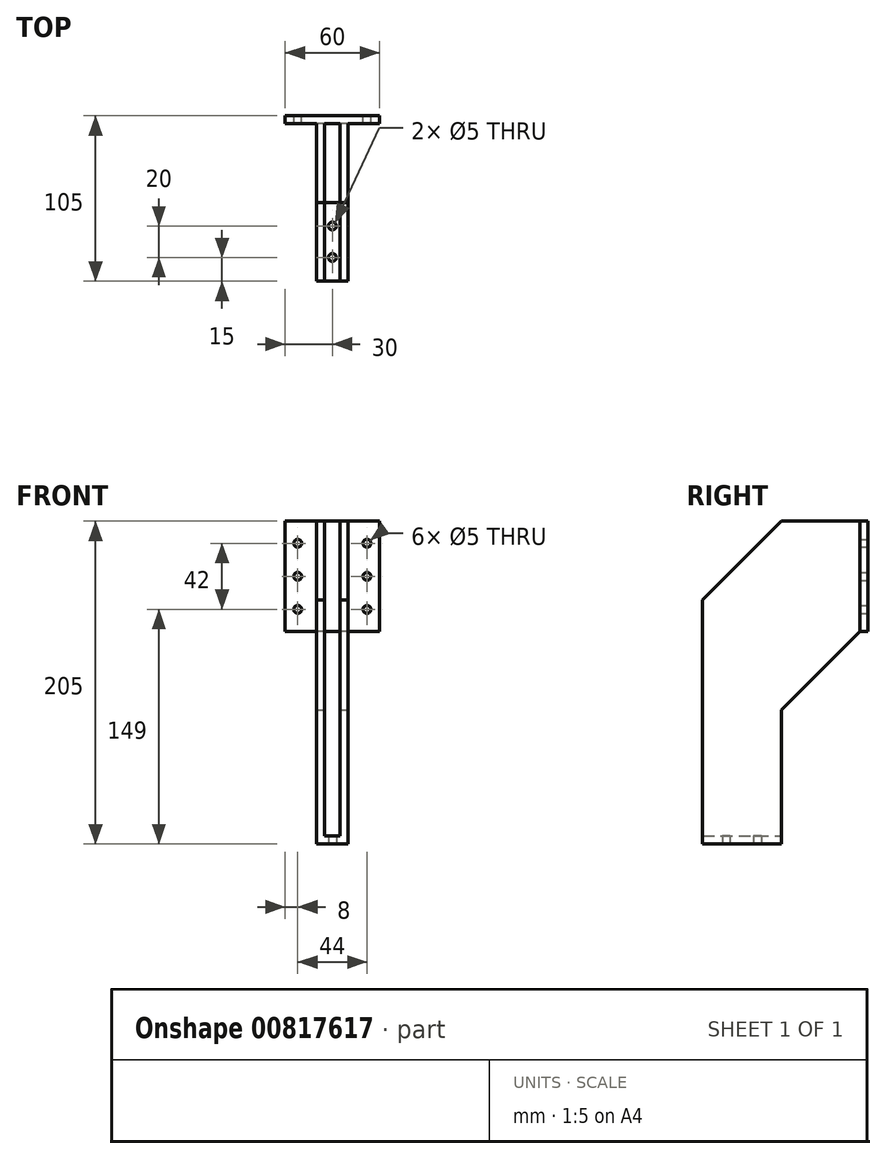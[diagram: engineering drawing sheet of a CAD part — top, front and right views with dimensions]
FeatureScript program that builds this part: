
annotation { "Feature Type Name" : "Feature", "Feature Type Description" : "" }
export const myFeature = defineFeature(function(context is Context, id is Id, definition is map)
    precondition{}
    {
        {
            var Q0;
            Q0=qCreatedBy(makeId("Front.planeOp"),FACE);
            var sketch = newSketch(context, id + "F0", { "sketchPlane" : qUnion([Q0])});
            skLineSegment(sketch, "E0.bottom", {"start": v(30, 35) * mm, "end": v(-30, 35) * mm});
            skLineSegment(sketch, "E0.top", {"start": v(30, -35) * mm, "end": v(-30, -35) * mm});
            skLineSegment(sketch, "E0.left", {"start": v(30, 35) * mm, "end": v(30, -35) * mm});
            skLineSegment(sketch, "E0.right", {"start": v(-30, 35) * mm, "end": v(-30, -35) * mm});
            skPoint(sketch, "E0.middle", {"position": v(0, 0) * mm});
            skCircle(sketch, "E1", {"center": v(-22, 21) * mm, "radius": 2.5 * mm});
            skCircle(sketch, "E2", {"center": v(-22, 0) * mm, "radius": 2.5 * mm});
            skCircle(sketch, "E3", {"center": v(-22, -21) * mm, "radius": 2.5 * mm});
            skCircle(sketch, "E4", {"center": v(22, 21) * mm, "radius": 2.5 * mm});
            skCircle(sketch, "E5", {"center": v(22, 0) * mm, "radius": 2.5 * mm});
            skCircle(sketch, "E6", {"center": v(22, -21) * mm, "radius": 2.5 * mm});
            skSolve(sketch);
        }
        {
            var Q0;
            Q0=makeQuery(id+"F0.imprint","IMPRINT",FACE,{"disambiguationData":[TD([[makeQuery(id+"F0.imprint","IMPRINT",EDGE,{"derivedFrom":sQuery(id+"F0.wireOp",EDGE,"E0.bottom")}),1.0]])]});
            extrude(context, id + "F1", {"entities" : qUnion([Q0]), "depth" : 5 * mm, "offsetDistance" : 25 * mm});
        }
        {
            var Q0;
            Q0=makeQuery(id+"F1.opExtrude","CAP_FACE",FACE,{"disambiguationData":[OSD([sQuery(id+"F0.wireOp",EDGE,"E0.bottom"),sQuery(id+"F0.wireOp",EDGE,"E0.top"),sQuery(id+"F0.wireOp",EDGE,"E0.left"),sQuery(id+"F0.wireOp",EDGE,"E0.right"),sQuery(id+"F0.wireOp",EDGE,"E1"),sQuery(id+"F0.wireOp",EDGE,"E2"),sQuery(id+"F0.wireOp",EDGE,"E3"),sQuery(id+"F0.wireOp",EDGE,"E4"),sQuery(id+"F0.wireOp",EDGE,"E5"),sQuery(id+"F0.wireOp",EDGE,"E6")])],"isStart":false});
            var sketch = newSketch(context, id + "F2", { "sketchPlane" : qUnion([Q0])});
            skLineSegment(sketch, "E7.bottom", {"start": v(-10, 35) * mm, "end": v(-5, 35) * mm});
            skLineSegment(sketch, "E7.top", {"start": v(-10, -165) * mm, "end": v(-5, -165) * mm});
            skLineSegment(sketch, "E7.left", {"start": v(-10, 35) * mm, "end": v(-10, -165) * mm});
            skLineSegment(sketch, "E7.right", {"start": v(-5, 35) * mm, "end": v(-5, -165) * mm});
            skLineSegment(sketch, "E8.bottom", {"start": v(5, 35) * mm, "end": v(10, 35) * mm});
            skLineSegment(sketch, "E8.top", {"start": v(5, -165) * mm, "end": v(10, -165) * mm});
            skLineSegment(sketch, "E8.left", {"start": v(5, 35) * mm, "end": v(5, -165) * mm});
            skLineSegment(sketch, "E8.right", {"start": v(10, 35) * mm, "end": v(10, -165) * mm});
            skSolve(sketch);
        }
        {
            var Q0;
            {var subQ0=sQuery(id+"F2.wireOp",EDGE,"E7.top");Q0=makeQuery(id+"F2.imprint","IMPRINT",FACE,{"disambiguationData":[TD([[makeQuery(id+"F2.imprint","IMPRINT",EDGE,{"derivedFrom":subQ0}),1.0]])]});}
            var Q1;
            {var subQ0=sQuery(id+"F2.wireOp",EDGE,"E7.bottom");Q1=makeQuery(id+"F2.imprint","IMPRINT",FACE,{"disambiguationData":[TD([[makeQuery(id+"F2.imprint","IMPRINT",EDGE,{"derivedFrom":subQ0}),-1.0]])]});}
            var Q2;
            {var subQ0=sQuery(id+"F2.wireOp",EDGE,"E8.bottom");Q2=makeQuery(id+"F2.imprint","IMPRINT",FACE,{"disambiguationData":[TD([[makeQuery(id+"F2.imprint","IMPRINT",EDGE,{"derivedFrom":subQ0}),-1.0]])]});}
            var Q3;
            {var subQ0=sQuery(id+"F2.wireOp",EDGE,"E8.top");Q3=makeQuery(id+"F2.imprint","IMPRINT",FACE,{"disambiguationData":[TD([[makeQuery(id+"F2.imprint","IMPRINT",EDGE,{"derivedFrom":subQ0}),1.0]])]});}
            var Q4;
            {var subQ0=sQuery(id+"F2.wireOp",EDGE,"E7.bottom");Q4=makeQuery(id+"F2.imprint","IMPRINT",FACE,{"disambiguationData":[TD([[makeQuery(id+"F2.imprint","IMPRINT",EDGE,{"derivedFrom":subQ0}),1.0]])]});}
            var Q5;
            {var subQ0=sQuery(id+"F2.wireOp",EDGE,"E8.bottom");Q5=makeQuery(id+"F2.imprint","IMPRINT",FACE,{"disambiguationData":[TD([[makeQuery(id+"F2.imprint","IMPRINT",EDGE,{"derivedFrom":subQ0}),1.0]])]});}
            extrude(context, id + "F3", {"entities" : qUnion([Q0, Q1, Q2, Q3, Q4, Q5]), "operationType" : NewBodyOperationType.ADD, "depth" : 100 * mm, "offsetDistance" : 25 * mm});
        }
        {
            var Q0;
            Q0=makeQuery(id+"F3.opExtrude","SWEPT_FACE",FACE,{"disambiguationData":[OSD([sQuery(id+"F2.wireOp",EDGE,"E8.right")])]});
            var sketch = newSketch(context, id + "F4", { "sketchPlane" : qUnion([Q0])});
            skPoint(sketch, "E9.start.orphan", {"position": v(-5, -35) * mm});
            skLineSegment(sketch, "E10", {"start": v(-55, 35) * mm, "end": v(-55, -165) * mm, "construction": true});
            skLineSegment(sketch, "E11", {"start": v(-105, -15) * mm, "end": v(-5, -15) * mm, "construction": true});
            skLineSegment(sketch, "E12", {"start": v(-55, 35) * mm, "end": v(-105, -15) * mm});
            skLineSegment(sketch, "E13", {"start": v(-105, -85) * mm, "end": v(-5, -85) * mm, "construction": true});
            skLineSegment(sketch, "E14", {"start": v(-5, -35) * mm, "end": v(-55, -85) * mm});
            skLineSegment(sketch, "E15", {"start": v(-55, -85) * mm, "end": v(-55, -165) * mm});
            skSolve(sketch);
        }
        {
            var Q0;
            {var subQ0=sQuery(id+"F4.wireOp",EDGE,"E12");Q0=makeQuery(id+"F4.imprint","IMPRINT",FACE,{"disambiguationData":[TD([[makeQuery(id+"F4.imprint","IMPRINT",EDGE,{"derivedFrom":subQ0}),-1.0]])]});}
            var Q1;
            Q1=makeQuery(id+"F4.imprint","IMPRINT",FACE,{"disambiguationData":[TD([[makeQuery(id+"F4.imprint","IMPRINT",EDGE,{"derivedFrom":sQuery(id+"F4.wireOp",EDGE,"E14")}),1.0]])]});
            extrude(context, id + "F5", {"entities" : qUnion([Q0, Q1]), "operationType" : NewBodyOperationType.REMOVE, "oppositeDirection" : true, "depth" : 25 * mm, "offsetDistance" : 25 * mm});
        }
        {
            var Q0;
            Q0=makeQuery(id+"F3.opExtrude","SWEPT_FACE",FACE,{"disambiguationData":[OSD([sQuery(id+"F2.wireOp",EDGE,"E8.top")])]});
            var sketch = newSketch(context, id + "F6", { "sketchPlane" : qUnion([Q0])});
            skLineSegment(sketch, "E16.bottom", {"start": v(10, 105) * mm, "end": v(-10, 105) * mm});
            skLineSegment(sketch, "E16.top", {"start": v(10, 55) * mm, "end": v(-10, 55) * mm});
            skLineSegment(sketch, "E16.left", {"start": v(10, 105) * mm, "end": v(10, 55) * mm});
            skLineSegment(sketch, "E16.right", {"start": v(-10, 105) * mm, "end": v(-10, 55) * mm});
            skSolve(sketch);
        }
        {
            var Q0;
            {var subQ2=sQuery(id+"F6.wireOp",EDGE,"E16.right");Q0=makeQuery(id+"F6.imprint","IMPRINT",FACE,{"disambiguationData":[TD([[makeQuery(id+"F6.imprint","IMPRINT",EDGE,{"derivedFrom":subQ2}),1.0]])]});}
            var Q1;
            {var subQ2=sQuery(id+"F6.wireOp",EDGE,"E16.left");Q1=makeQuery(id+"F6.imprint","IMPRINT",FACE,{"disambiguationData":[TD([[makeQuery(id+"F6.imprint","IMPRINT",EDGE,{"derivedFrom":subQ2}),-1.0]])]});}
            extrude(context, id + "F7", {"entities" : qUnion([Q0, Q1]), "operationType" : NewBodyOperationType.ADD, "depth" : 5 * mm, "offsetDistance" : 25 * mm});
        }
        {
            var Q0;
            Q0=makeQuery(id+"F7.opExtrude","CAP_FACE",FACE,{"disambiguationData":[OSD([sQuery(id+"F6.wireOp",EDGE,"E16.bottom"),sQuery(id+"F6.wireOp",EDGE,"E16.top"),sQuery(id+"F6.wireOp",EDGE,"E16.left"),sQuery(id+"F6.wireOp",EDGE,"E16.right")])],"isStart":false});
            var sketch = newSketch(context, id + "F8", { "sketchPlane" : qUnion([Q0])});
            skPoint(sketch, "E17", {"position": v(0, 70) * mm});
            skPoint(sketch, "E17.positionSnap0", {"position": v(0, 55) * mm});
            skPoint(sketch, "E18", {"position": v(0, 90) * mm});
            skSolve(sketch);
        }
        {
            var Q0;
            Q0=sQuery(id+"F8.wireOp",VERTEX,"E18");
            var Q1;
            Q1=sQuery(id+"F8.wireOp",VERTEX,"E17");
            var Q2;
            Q2=makeQuery(id+"F1.opExtrude","SWEPT_BODY",BODY,{"disambiguationData":[OSD([sQuery(id+"F0.wireOp",EDGE,"E0.bottom"),sQuery(id+"F0.wireOp",EDGE,"E0.top"),sQuery(id+"F0.wireOp",EDGE,"E0.left"),sQuery(id+"F0.wireOp",EDGE,"E0.right"),sQuery(id+"F0.wireOp",EDGE,"E1"),sQuery(id+"F0.wireOp",EDGE,"E2"),sQuery(id+"F0.wireOp",EDGE,"E3"),sQuery(id+"F0.wireOp",EDGE,"E4"),sQuery(id+"F0.wireOp",EDGE,"E5"),sQuery(id+"F0.wireOp",EDGE,"E6")])]});
            hole(context, id + "F9", {"style" : HoleStyle.SIMPLE, "endStyle" : HoleEndStyle.BLIND, "holeDiameter" : 5 * mm, "majorDiameter" : 5 * mm, "holeDepth" : 40 * mm, "tappedDepth" : 12 * mm, "tapClearance" : 3, "locations" : qUnion([Q0, Q1]), "scope" : qUnion([Q2])});
        }
    });
